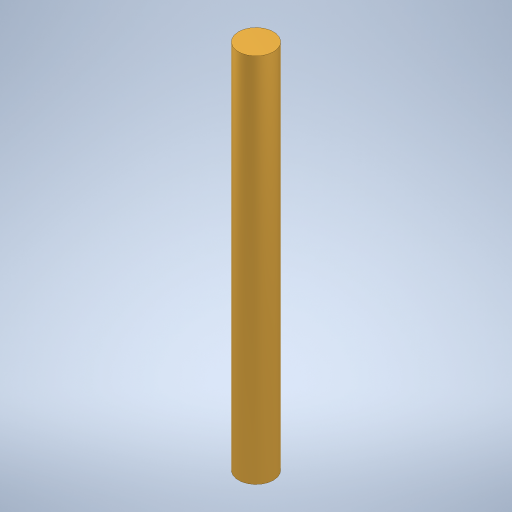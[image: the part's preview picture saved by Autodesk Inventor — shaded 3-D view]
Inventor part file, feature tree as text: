
AUTODESK INVENTOR PART (.ipt)
format: ipt  version: 2023 (Build 270158000, 158)  size: 242,176 bytes
history: native  units: mm
features: other x1, extrude x1, sketch x1
ambient origin geometry x8: Origin, YZ Plane, XZ Plane, XY Plane, X Axis, Y Axis, Z Axis, Center Point
bodies: Body1 (feature_tree)
feature tree (3):
  other  "Sólido1"
  extrude  "Extrusão1"  Depth=85.0mm TaperAngle=0.0deg
  sketch  "Esboço1"  dims[d1=8.0mm d2=85.0mm d3=0.0mm]
